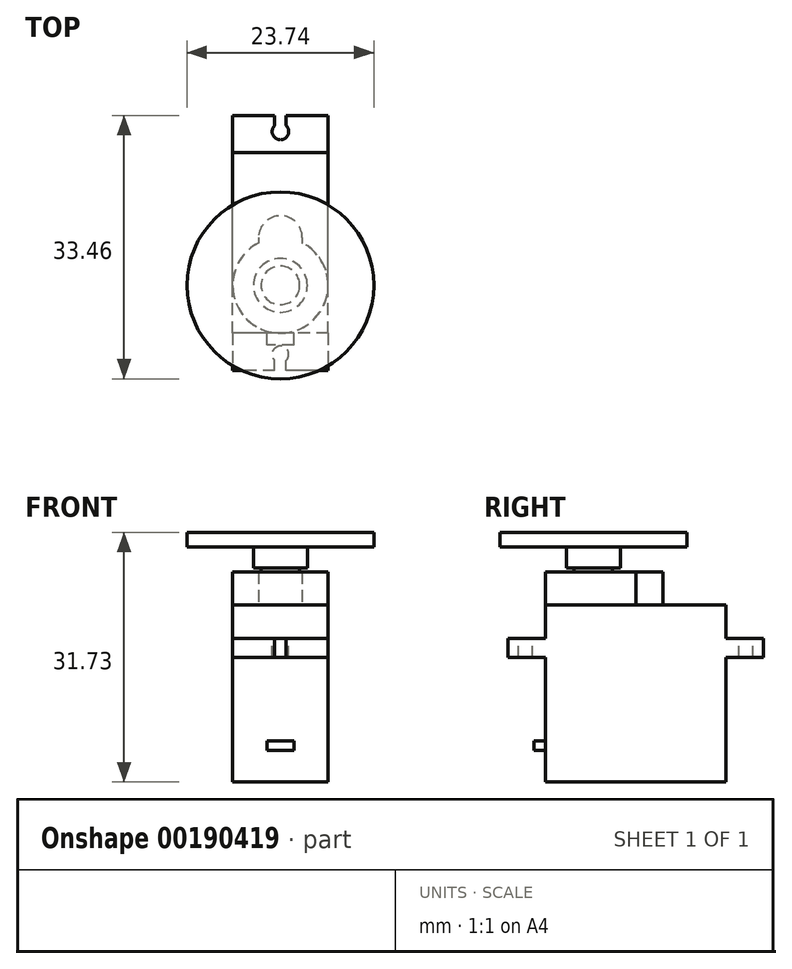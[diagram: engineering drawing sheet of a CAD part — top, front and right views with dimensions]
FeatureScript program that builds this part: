
annotation { "Feature Type Name" : "Feature", "Feature Type Description" : "" }
export const myFeature = defineFeature(function(context is Context, id is Id, definition is map)
    precondition{}
    {
        {
            var Q0;
            Q0=qCreatedBy(makeId("Top.planeOp"),FACE);
            var sketch = newSketch(context, id + "F0", { "sketchPlane" : qUnion([Q0])});
            skLineSegment(sketch, "E0.bottom", {"start": v(6.06, -11.45) * mm, "end": v(-6.07, -11.45) * mm});
            skLineSegment(sketch, "E0.top", {"start": v(6.06, 11.45) * mm, "end": v(-6.07, 11.45) * mm});
            skLineSegment(sketch, "E0.left", {"start": v(6.06, -11.45) * mm, "end": v(6.07, 11.45) * mm});
            skLineSegment(sketch, "E0.right", {"start": v(-6.07, -11.45) * mm, "end": v(-6.06, 11.45) * mm});
            skPoint(sketch, "E0.middle", {"position": v(0, 0) * mm});
            skLineSegment(sketch, "E1", {"start": v(-6.07, 0) * mm, "end": v(6.07, 0) * mm, "construction": true});
            skSolve(sketch);
        }
        {
            var Q0;
            Q0 = qSketchRegion(id + "F0", true);
            extrude(context, id + "F1", {"entities" : qUnion([Q0]), "depth" : 22.53 * mm});
        }
        {
            var Q0;
            Q0=makeQuery(id+"F1.opExtrude","SWEPT_FACE",FACE,{"disambiguationData":[OSD([sQuery(id+"F0.wireOp",EDGE,"E0.top")])]});
            var sketch = newSketch(context, id + "F2", { "sketchPlane" : qUnion([Q0])});
            skLineSegment(sketch, "E2.bottom", {"start": v(-6.07, 18.23) * mm, "end": v(6.07, 18.23) * mm});
            skLineSegment(sketch, "E2.top", {"start": v(-6.07, 15.81) * mm, "end": v(6.07, 15.81) * mm});
            skLineSegment(sketch, "E2.left", {"start": v(-6.07, 18.23) * mm, "end": v(-6.07, 15.81) * mm});
            skLineSegment(sketch, "E2.right", {"start": v(6.07, 18.23) * mm, "end": v(6.07, 15.81) * mm});
            skSolve(sketch);
        }
        {
            var Q0;
            Q0=makeQuery(id+"F2.imprint","IMPRINT",FACE,{"disambiguationData":[TD([[makeQuery(id+"F2.imprint","IMPRINT",EDGE,{"derivedFrom":sQuery(id+"F2.wireOp",EDGE,"E2.bottom")}),-1.0]])]});
            extrude(context, id + "F3", {"entities" : qUnion([Q0]), "operationType" : NewBodyOperationType.ADD, "depth" : 4.75 * mm, "hasSecondDirection" : true, "secondDirectionOppositeDirection" : true, "secondDirectionDepth" : (22.9 + 4.75) * mm});
        }
        {
            var Q0;
            Q0=makeQuery(id+"F3.opExtrude","SWEPT_FACE",FACE,{"disambiguationData":[OSD([sQuery(id+"F2.wireOp",EDGE,"E2.bottom")])]});
            var sketch = newSketch(context, id + "F4", { "sketchPlane" : qUnion([Q0])});
            skCircle(sketch, "E3", {"center": v(0, 14.15) * mm, "radius": 1.05 * mm});
            skLineSegment(sketch, "E4", {"start": v(0, 16.2) * mm, "end": v(0, -16.2) * mm});
            skLineSegment(sketch, "E5", {"start": v(6.06, 15.2) * mm, "end": v(-6.06, 15.2) * mm});
            skLineSegment(sketch, "E6.bottom", {"start": v(-0.73, 16.2) * mm, "end": v(0.72, 16.2) * mm});
            skLineSegment(sketch, "E6.top", {"start": v(-0.73, 14.2) * mm, "end": v(0.72, 14.2) * mm});
            skLineSegment(sketch, "E6.left", {"start": v(-0.73, 16.2) * mm, "end": v(-0.73, 14.2) * mm});
            skLineSegment(sketch, "E6.right", {"start": v(0.72, 16.2) * mm, "end": v(0.72, 14.2) * mm});
            skPoint(sketch, "E6.middle", {"position": v(0, 15.2) * mm});
            skLineSegment(sketch, "E7.MirrorCS", {"start": v(-0.73, -14.2) * mm, "end": v(0.72, -14.2) * mm});
            skLineSegment(sketch, "E8.MirrorCS", {"start": v(-0.73, -16.2) * mm, "end": v(0.72, -16.2) * mm});
            skLineSegment(sketch, "E9.MirrorCS", {"start": v(0, -16.2) * mm, "end": v(0, 16.2) * mm});
            skPoint(sketch, "E10.MirrorP", {"position": v(0, -15.2) * mm});
            skCircle(sketch, "E11.MirrorC", {"center": v(0, -14.15) * mm, "radius": 1.05 * mm});
            skLineSegment(sketch, "E12.MirrorCS", {"start": v(-0.73, -16.2) * mm, "end": v(-0.73, -14.2) * mm});
            skLineSegment(sketch, "E13.MirrorCS", {"start": v(0.72, -16.2) * mm, "end": v(0.72, -14.2) * mm});
            skLineSegment(sketch, "E14.MirrorCS", {"start": v(6.06, -15.2) * mm, "end": v(-6.06, -15.2) * mm});
            skSolve(sketch);
        }
        {
            var Q0;
            {var subQ0=sQuery(id+"F4.wireOp",EDGE,"E6.right");var subQ1=sQuery(id+"F4.wireOp",EDGE,"E3");var subQ2=makeQuery(id+"F4.imprint","INTERSECT",VERTEX,{"derivedFrom":[subQ1,subQ0]});Q0=makeQuery(id+"F4.imprint","IMPRINT",FACE,{"disambiguationData":[TD([[makeQuery(id+"F4.imprint","IMPRINT",EDGE,{"disambiguationData":[TD([[subQ2,1.0]])],"derivedFrom":subQ1}),1.0]])]});}
            var Q1;
            {var subQ0=sQuery(id+"F4.wireOp",EDGE,"E6.left");var subQ1=sQuery(id+"F4.wireOp",EDGE,"E3");var subQ2=makeQuery(id+"F4.imprint","INTERSECT",VERTEX,{"derivedFrom":[subQ1,subQ0]});Q1=makeQuery(id+"F4.imprint","IMPRINT",FACE,{"disambiguationData":[TD([[makeQuery(id+"F4.imprint","IMPRINT",EDGE,{"disambiguationData":[TD([[subQ2,-1.0]])],"derivedFrom":subQ1}),1.0]])]});}
            var Q2;
            {var subQ0=sQuery(id+"F4.wireOp",EDGE,"E6.left");var subQ5=sQuery(id+"F4.wireOp",EDGE,"E6.top");var subQ6=makeQuery(id+"F4.imprint","INTERSECT",VERTEX,{"derivedFrom":[subQ5,subQ0]});Q2=makeQuery(id+"F4.imprint","IMPRINT",FACE,{"disambiguationData":[TD([[makeQuery(id+"F4.imprint","IMPRINT",EDGE,{"disambiguationData":[TD([[subQ6,-1.0]])],"derivedFrom":subQ5}),1.0]])]});}
            var Q3;
            {var subQ0=sQuery(id+"F4.wireOp",EDGE,"E6.right");var subQ5=sQuery(id+"F4.wireOp",EDGE,"E6.top");var subQ6=makeQuery(id+"F4.imprint","INTERSECT",VERTEX,{"derivedFrom":[subQ5,subQ0]});Q3=makeQuery(id+"F4.imprint","IMPRINT",FACE,{"disambiguationData":[TD([[makeQuery(id+"F4.imprint","IMPRINT",EDGE,{"disambiguationData":[TD([[subQ6,1.0]])],"derivedFrom":subQ5}),1.0]])]});}
            var Q4;
            {var subQ0=sQuery(id+"F4.wireOp",EDGE,"E6.right");var subQ1=sQuery(id+"F4.wireOp",EDGE,"E3");var subQ2=makeQuery(id+"F4.imprint","INTERSECT",VERTEX,{"derivedFrom":[subQ1,subQ0]});Q4=makeQuery(id+"F4.imprint","IMPRINT",FACE,{"disambiguationData":[TD([[makeQuery(id+"F4.imprint","IMPRINT",EDGE,{"disambiguationData":[TD([[subQ2,1.0]])],"derivedFrom":subQ0}),-1.0]])]});}
            var Q5;
            {var subQ0=sQuery(id+"F4.wireOp",EDGE,"E6.right");var subQ1=sQuery(id+"F4.wireOp",EDGE,"E5");var subQ2=makeQuery(id+"F4.imprint","INTERSECT",VERTEX,{"derivedFrom":[subQ1,subQ0]});Q5=makeQuery(id+"F4.imprint","IMPRINT",FACE,{"disambiguationData":[TD([[makeQuery(id+"F4.imprint","IMPRINT",EDGE,{"disambiguationData":[TD([[subQ2,-1.0]])],"derivedFrom":subQ1}),-1.0]])]});}
            var Q6;
            {var subQ0=sQuery(id+"F4.wireOp",EDGE,"E6.left");var subQ1=sQuery(id+"F4.wireOp",EDGE,"E5");var subQ2=makeQuery(id+"F4.imprint","INTERSECT",VERTEX,{"derivedFrom":[subQ1,subQ0]});Q6=makeQuery(id+"F4.imprint","IMPRINT",FACE,{"disambiguationData":[TD([[makeQuery(id+"F4.imprint","IMPRINT",EDGE,{"disambiguationData":[TD([[subQ2,1.0]])],"derivedFrom":subQ1}),-1.0]])]});}
            var Q7;
            {var subQ0=sQuery(id+"F4.wireOp",EDGE,"E6.left");var subQ1=sQuery(id+"F4.wireOp",EDGE,"E3");var subQ2=makeQuery(id+"F4.imprint","INTERSECT",VERTEX,{"derivedFrom":[subQ1,subQ0]});Q7=makeQuery(id+"F4.imprint","IMPRINT",FACE,{"disambiguationData":[TD([[makeQuery(id+"F4.imprint","IMPRINT",EDGE,{"disambiguationData":[TD([[subQ2,1.0]])],"derivedFrom":subQ0}),1.0]])]});}
            extrude(context, id + "F5", {"entities" : qUnion([Q0, Q1, Q2, Q3, Q4, Q5, Q6, Q7]), "operationType" : NewBodyOperationType.REMOVE, "oppositeDirection" : true, "depth" : 25 * mm});
        }
        {
            var Q0;
            {var subQ0=sQuery(id+"F4.wireOp",EDGE,"E13.MirrorCS");var subQ1=sQuery(id+"F4.wireOp",EDGE,"E7.MirrorCS");var subQ2=makeQuery(id+"F4.imprint","INTERSECT",VERTEX,{"derivedFrom":[subQ1,subQ0]});Q0=makeQuery(id+"F4.imprint","IMPRINT",FACE,{"disambiguationData":[TD([[makeQuery(id+"F4.imprint","IMPRINT",EDGE,{"disambiguationData":[TD([[subQ2,1.0]])],"derivedFrom":subQ1}),1.0]])]});}
            var Q1;
            {var subQ0=sQuery(id+"F4.wireOp",EDGE,"E12.MirrorCS");var subQ1=sQuery(id+"F4.wireOp",EDGE,"E7.MirrorCS");var subQ2=makeQuery(id+"F4.imprint","INTERSECT",VERTEX,{"derivedFrom":[subQ1,subQ0]});Q1=makeQuery(id+"F4.imprint","IMPRINT",FACE,{"disambiguationData":[TD([[makeQuery(id+"F4.imprint","IMPRINT",EDGE,{"disambiguationData":[TD([[subQ2,-1.0]])],"derivedFrom":subQ1}),1.0]])]});}
            var Q2;
            {var subQ0=sQuery(id+"F4.wireOp",EDGE,"E13.MirrorCS");var subQ1=sQuery(id+"F4.wireOp",EDGE,"E7.MirrorCS");var subQ2=makeQuery(id+"F4.imprint","INTERSECT",VERTEX,{"derivedFrom":[subQ1,subQ0]});Q2=makeQuery(id+"F4.imprint","IMPRINT",FACE,{"disambiguationData":[TD([[makeQuery(id+"F4.imprint","IMPRINT",EDGE,{"disambiguationData":[TD([[subQ2,1.0]])],"derivedFrom":subQ1}),-1.0]])]});}
            var Q3;
            {var subQ0=sQuery(id+"F4.wireOp",EDGE,"E13.MirrorCS");var subQ1=sQuery(id+"F4.wireOp",EDGE,"E11.MirrorC");var subQ2=makeQuery(id+"F4.imprint","INTERSECT",VERTEX,{"derivedFrom":[subQ1,subQ0]});Q3=makeQuery(id+"F4.imprint","IMPRINT",FACE,{"disambiguationData":[TD([[makeQuery(id+"F4.imprint","IMPRINT",EDGE,{"disambiguationData":[TD([[subQ2,1.0]])],"derivedFrom":subQ0}),1.0]])]});}
            var Q4;
            {var subQ1=sQuery(id+"F4.wireOp",EDGE,"E8.MirrorCS");var subQ3=sQuery(id+"F4.wireOp",EDGE,"E9.MirrorCS");var subQ4=makeQuery(id+"F4.imprint","INTERSECT",VERTEX,{"derivedFrom":[subQ1,subQ3]});Q4=makeQuery(id+"F4.imprint","IMPRINT",FACE,{"disambiguationData":[TD([[makeQuery(id+"F4.imprint","IMPRINT",EDGE,{"disambiguationData":[TD([[subQ4,1.0]])],"derivedFrom":subQ1}),-1.0]])]});}
            var Q5;
            {var subQ1=sQuery(id+"F4.wireOp",EDGE,"E8.MirrorCS");var subQ3=sQuery(id+"F4.wireOp",EDGE,"E9.MirrorCS");var subQ4=makeQuery(id+"F4.imprint","INTERSECT",VERTEX,{"derivedFrom":[subQ1,subQ3]});Q5=makeQuery(id+"F4.imprint","IMPRINT",FACE,{"disambiguationData":[TD([[makeQuery(id+"F4.imprint","IMPRINT",EDGE,{"disambiguationData":[TD([[subQ4,-1.0]])],"derivedFrom":subQ1}),-1.0]])]});}
            var Q6;
            {var subQ0=sQuery(id+"F4.wireOp",EDGE,"E12.MirrorCS");var subQ1=sQuery(id+"F4.wireOp",EDGE,"E7.MirrorCS");var subQ2=makeQuery(id+"F4.imprint","INTERSECT",VERTEX,{"derivedFrom":[subQ1,subQ0]});Q6=makeQuery(id+"F4.imprint","IMPRINT",FACE,{"disambiguationData":[TD([[makeQuery(id+"F4.imprint","IMPRINT",EDGE,{"disambiguationData":[TD([[subQ2,-1.0]])],"derivedFrom":subQ1}),-1.0]])]});}
            var Q7;
            {var subQ0=sQuery(id+"F4.wireOp",EDGE,"E12.MirrorCS");var subQ1=sQuery(id+"F4.wireOp",EDGE,"E11.MirrorC");var subQ2=makeQuery(id+"F4.imprint","INTERSECT",VERTEX,{"derivedFrom":[subQ1,subQ0]});Q7=makeQuery(id+"F4.imprint","IMPRINT",FACE,{"disambiguationData":[TD([[makeQuery(id+"F4.imprint","IMPRINT",EDGE,{"disambiguationData":[TD([[subQ2,1.0]])],"derivedFrom":subQ0}),-1.0]])]});}
            extrude(context, id + "F6", {"entities" : qUnion([Q0, Q1, Q2, Q3, Q4, Q5, Q6, Q7]), "operationType" : NewBodyOperationType.REMOVE, "oppositeDirection" : true, "depth" : 25 * mm});
        }
        {
            var Q0;
            Q0=makeQuery(id+"F1.opExtrude","CAP_FACE",FACE,{"disambiguationData":[OSD([sQuery(id+"F0.wireOp",EDGE,"E0.bottom"),sQuery(id+"F0.wireOp",EDGE,"E0.top"),sQuery(id+"F0.wireOp",EDGE,"E0.left"),sQuery(id+"F0.wireOp",EDGE,"E0.right")])],"isStart":false});
            var sketch = newSketch(context, id + "F7", { "sketchPlane" : qUnion([Q0])});
            skCircle(sketch, "E15", {"center": v(0, -5.38) * mm, "radius": 6.07 * mm});
            skCircle(sketch, "E16", {"center": v(0, 0.68) * mm, "radius": 2.77 * mm});
            skLineSegment(sketch, "E17", {"start": v(2.77, 0.68) * mm, "end": v(2.77, 0.01) * mm});
            skLineSegment(sketch, "E18", {"start": v(-2.77, 0.68) * mm, "end": v(-2.77, 0.01) * mm});
            skSolve(sketch);
        }
        {
            var Q0;
            Q0 = qSketchRegion(id + "F7", true);
            var Q1;
            {var subQ0=sQuery(id+"F7.wireOp",EDGE,"E16");var subQ1=sQuery(id+"F7.wireOp",EDGE,"E15");var subQ2=makeQuery(id+"F7.imprint","INTERSECT",VERTEX,{"disambiguationData":[OD(0.0)],"derivedFrom":[subQ1,subQ0]});Q1=makeQuery(id+"F7.imprint","IMPRINT",FACE,{"disambiguationData":[TD([[makeQuery(id+"F7.imprint","IMPRINT",EDGE,{"disambiguationData":[TD([[subQ2,-1.0]])],"derivedFrom":subQ1}),1.0]])]});}
            extrude(context, id + "F8", {"entities" : qUnion([Q0, Q1]), "operationType" : NewBodyOperationType.ADD, "depth" : 4.15 * mm});
        }
        {
            var Q0;
            Q0=makeQuery(id+"F8.opExtrude","CAP_FACE",FACE,{"disambiguationData":[OSD([sQuery(id+"F7.wireOp",EDGE,"E15"),sQuery(id+"F7.wireOp",EDGE,"E16"),sQuery(id+"F7.wireOp",EDGE,"E17"),sQuery(id+"F7.wireOp",EDGE,"E18")])],"isStart":false});
            var sketch = newSketch(context, id + "F9", { "sketchPlane" : qUnion([Q0])});
            skCircle(sketch, "E19", {"center": v(0, -5.38) * mm, "radius": 2.45 * mm});
            skSolve(sketch);
        }
        {
            var Q0;
            Q0 = qSketchRegion(id + "F9", true);
            extrude(context, id + "F10", {"entities" : qUnion([Q0]), "operationType" : NewBodyOperationType.ADD, "depth" : 3.2 * mm});
        }
        {
            var Q0;
            Q0=makeQuery(id+"F10.opExtrude","CAP_FACE",FACE,{"disambiguationData":[OSD([sQuery(id+"F9.wireOp",EDGE,"E19")])],"isStart":false});
            var sketch = newSketch(context, id + "F11", { "sketchPlane" : qUnion([Q0])});
            skCircle(sketch, "E20", {"center": v(0, -5.38) * mm, "radius": 11.87 * mm});
            skCircle(sketch, "E21", {"center": v(0, -5.38) * mm, "radius": 3.43 * mm});
            skSolve(sketch);
        }
        {
            var Q0;
            Q0 = qSketchRegion(id + "F11", true);
            var Q1;
            Q1=makeQuery(id+"F11.imprint","IMPRINT",FACE,{"disambiguationData":[TD([[makeQuery(id+"F11.imprint","IMPRINT",EDGE,{"derivedFrom":sQuery(id+"F11.wireOp",EDGE,"E21")}),1.0]])]});
            var Q2;
            Q2=makeQuery(id+"F11.imprint","IMPRINT",FACE,{"disambiguationData":[TD([[makeQuery(id+"F11.imprint","IMPRINT",EDGE,{"derivedFrom":makeQuery(id+"F10.opExtrude","CAP_EDGE",EDGE,{"disambiguationData":[OSD([sQuery(id+"F9.wireOp",EDGE,"E19")])],"isStart":false})}),1.0]])]});
            extrude(context, id + "F12", {"entities" : qUnion([Q0, Q1, Q2]), "depth" : 1.85 * mm});
        }
        {
            var Q0;
            Q0=makeQuery(id+"F11.imprint","IMPRINT",FACE,{"disambiguationData":[TD([[makeQuery(id+"F11.imprint","IMPRINT",EDGE,{"derivedFrom":sQuery(id+"F11.wireOp",EDGE,"E21")}),1.0]])]});
            extrude(context, id + "F13", {"entities" : qUnion([Q0]), "operationType" : NewBodyOperationType.ADD, "oppositeDirection" : true, "depth" : (4.5 - 1.83) * mm});
        }
        {
            var Q0;
            {var subQ2=sQuery(id+"F0.wireOp",EDGE,"E0.bottom");Q0=makeQuery(id+"F3.boolean.opBoolean","SPLIT",FACE,{"disambiguationData":[TD([makeQuery(id+"F3.opExtrude","SWEPT_FACE",FACE,{"disambiguationData":[OSD([sQuery(id+"F2.wireOp",EDGE,"E2.top")])]})])],"derivedFrom":makeQuery(id+"F1.opExtrude","SWEPT_FACE",FACE,{"disambiguationData":[OSD([subQ2])]})});}
            var sketch = newSketch(context, id + "F14", { "sketchPlane" : qUnion([Q0])});
            skLineSegment(sketch, "E22", {"start": v(0, 0) * mm, "end": v(0, 15.81) * mm});
            skLineSegment(sketch, "E23.bottom", {"start": v(1.7, 4) * mm, "end": v(-1.7, 4) * mm});
            skLineSegment(sketch, "E23.top", {"start": v(1.7, 5.2) * mm, "end": v(-1.7, 5.2) * mm});
            skLineSegment(sketch, "E23.left", {"start": v(1.7, 4) * mm, "end": v(1.7, 5.2) * mm});
            skLineSegment(sketch, "E23.right", {"start": v(-1.7, 4) * mm, "end": v(-1.7, 5.2) * mm});
            skPoint(sketch, "E23.middle", {"position": v(0, 4.6) * mm});
            skSolve(sketch);
        }
        {
            var Q0;
            Q0 = qSketchRegion(id + "F14", true);
            extrude(context, id + "F15", {"entities" : qUnion([Q0]), "operationType" : NewBodyOperationType.ADD, "depth" : 1.5 * mm});
        }
    });
